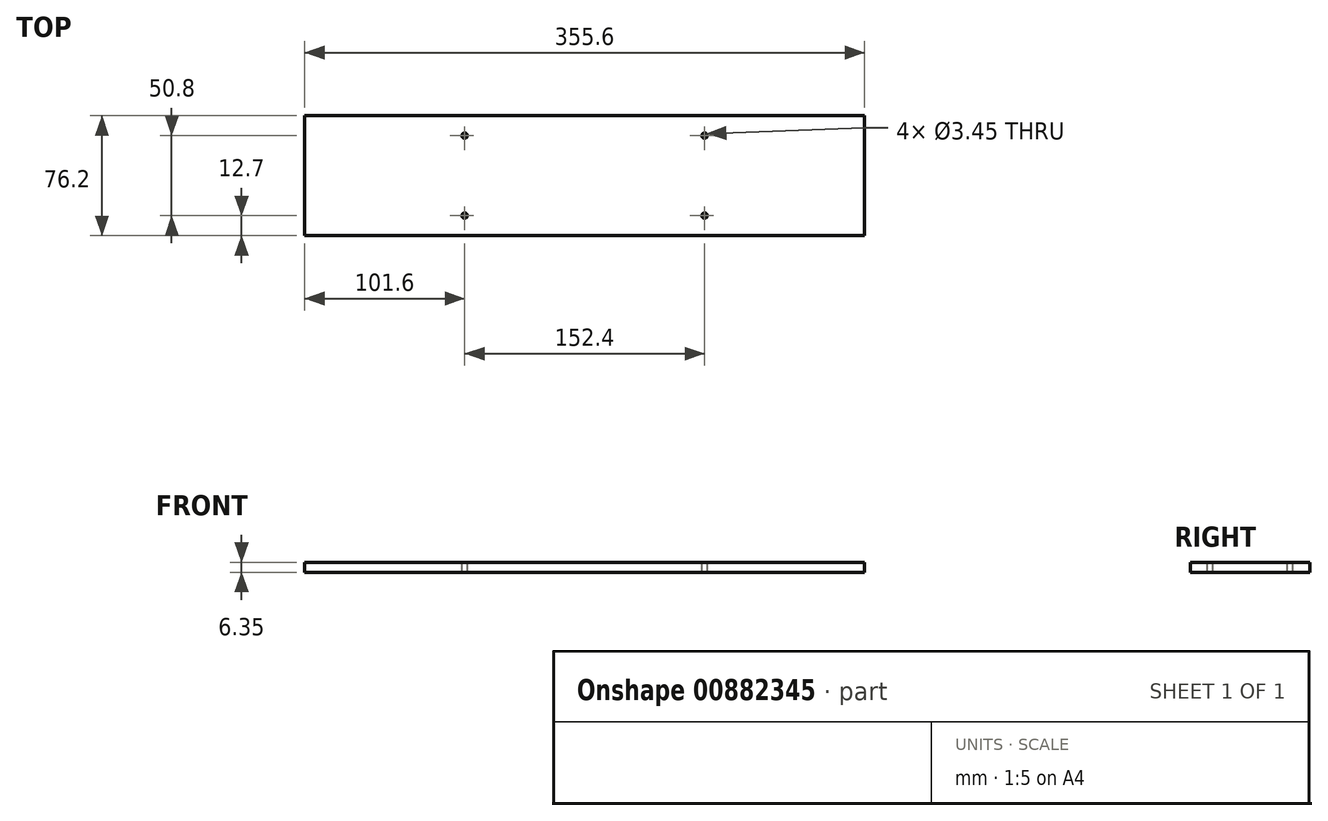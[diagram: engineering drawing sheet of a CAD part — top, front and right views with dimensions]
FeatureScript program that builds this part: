
annotation { "Feature Type Name" : "Feature", "Feature Type Description" : "" }
export const myFeature = defineFeature(function(context is Context, id is Id, definition is map)
    precondition{}
    {
        {
            var Q0;
            Q0=qCreatedBy(makeId("Top.planeOp"),FACE);
            var sketch = newSketch(context, id + "F0", { "sketchPlane" : qUnion([Q0])});
            skLineSegment(sketch, "E0.bottom", {"start": v(0, 0) * mm, "end": v(-355.6, 0) * mm});
            skLineSegment(sketch, "E0.top", {"start": v(0, 76.2) * mm, "end": v(-355.6, 76.2) * mm});
            skLineSegment(sketch, "E0.left", {"start": v(0, 0) * mm, "end": v(0, 76.2) * mm});
            skLineSegment(sketch, "E0.right", {"start": v(-355.6, 0) * mm, "end": v(-355.6, 76.2) * mm});
            skSolve(sketch);
        }
        {
            var Q0;
            Q0 = qSketchRegion(id + "F0", true);
            extrude(context, id + "F1", {"entities" : qUnion([Q0]), "depth" : 6.35 * mm, "offsetDistance" : 25.4 * mm});
        }
        {
            var Q0;
            Q0=makeQuery(id+"F1.opExtrude","CAP_FACE",FACE,{"disambiguationData":[OSD([sQuery(id+"F0.wireOp",EDGE,"E0.bottom"),sQuery(id+"F0.wireOp",EDGE,"E0.top"),sQuery(id+"F0.wireOp",EDGE,"E0.left"),sQuery(id+"F0.wireOp",EDGE,"E0.right")])],"isStart":false});
            var sketch = newSketch(context, id + "F2", { "sketchPlane" : qUnion([Q0])});
            skPoint(sketch, "E1", {"position": v(-254, 63.5) * mm});
            skPoint(sketch, "E2", {"position": v(-101.6, 63.5) * mm});
            skPoint(sketch, "E3", {"position": v(-254, 12.7) * mm});
            skPoint(sketch, "E4", {"position": v(-101.6, 12.7) * mm});
            skSolve(sketch);
        }
        {
            var Q0;
            Q0=sQuery(id+"F2.wireOp",VERTEX,"E1");
            var Q1;
            Q1=sQuery(id+"F2.wireOp",VERTEX,"E3");
            var Q2;
            Q2=sQuery(id+"F2.wireOp",VERTEX,"E4");
            var Q3;
            Q3=sQuery(id+"F2.wireOp",VERTEX,"E2");
            var Q4;
            Q4=makeQuery(id+"F1.opExtrude","SWEPT_BODY",BODY,{"disambiguationData":[OSD([sQuery(id+"F0.wireOp",EDGE,"E0.bottom"),sQuery(id+"F0.wireOp",EDGE,"E0.top"),sQuery(id+"F0.wireOp",EDGE,"E0.left"),sQuery(id+"F0.wireOp",EDGE,"E0.right")])]});
            hole(context, id + "F3", {"style" : HoleStyle.SIMPLE, "endStyle" : HoleEndStyle.THROUGH, "standardTappedOrClearance" : lookupTablePath({ "standard" : "ANSI", "engagement" : "75%", "pitch" : "32 tpi", "size" : "#8", "type" : "Tapped" }), "standardBlindInLast" : lookupTablePath({ "standard" : "ANSI", "engagement" : "75%", "pitch" : "32 tpi", "size" : "#8", "type" : "Tapped" }), "holeDiameter" : 3.45 * mm, "majorDiameter" : 4.17 * mm, "showTappedDepth" : true, "isTappedThrough" : true, "tappedDepth" : 12.7 * mm, "tapClearance" : 3, "locations" : qUnion([Q0, Q1, Q2, Q3]), "scope" : qUnion([Q4])});
        }
    });
